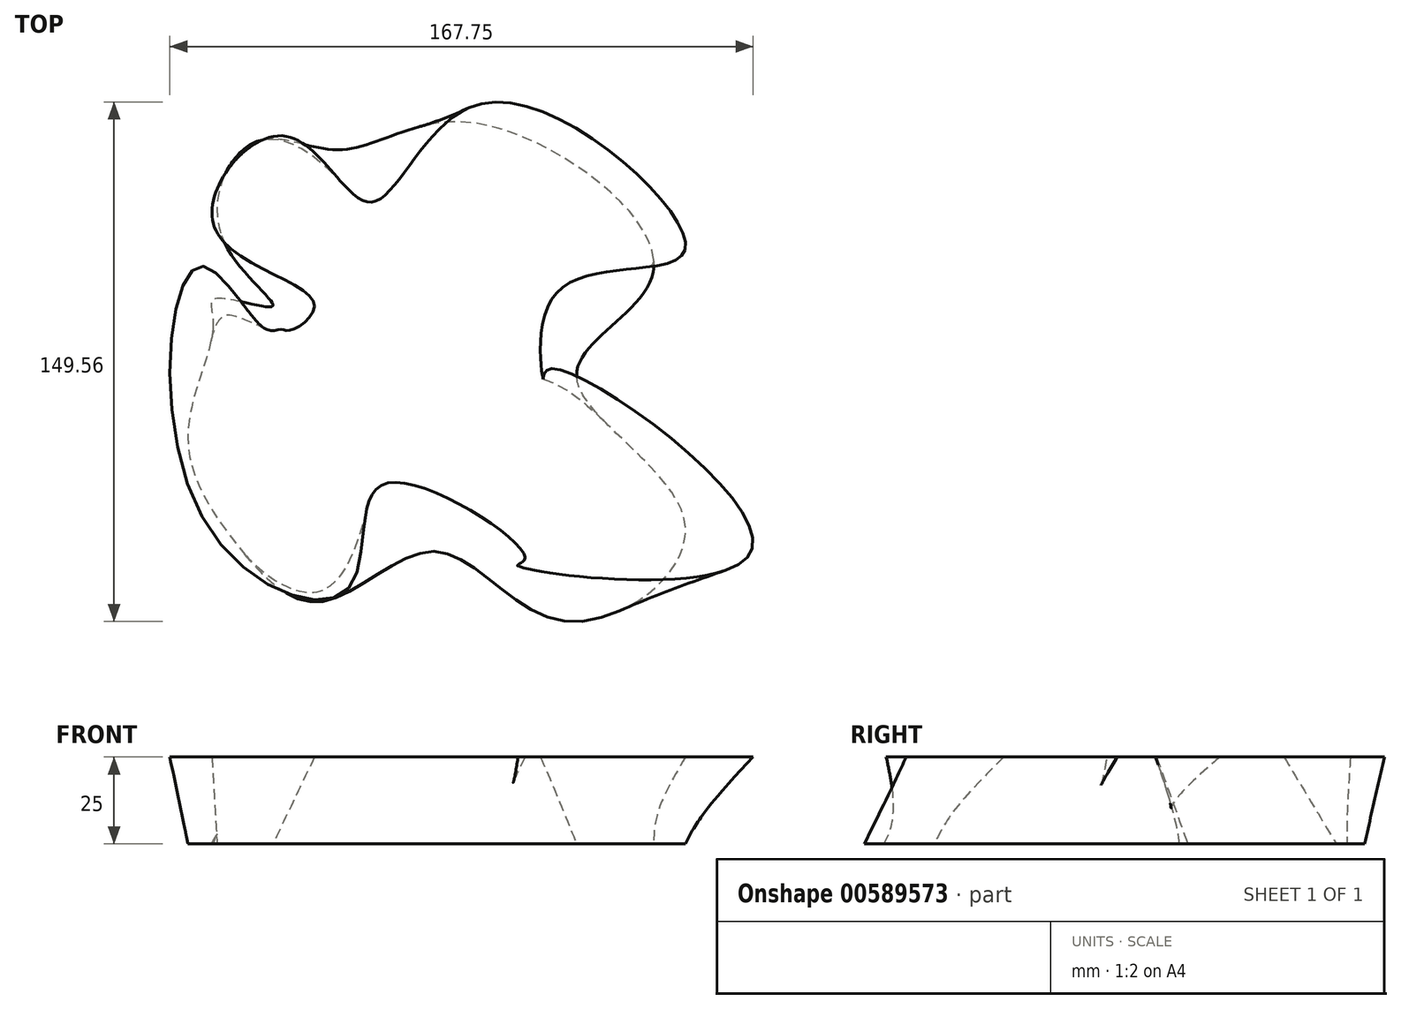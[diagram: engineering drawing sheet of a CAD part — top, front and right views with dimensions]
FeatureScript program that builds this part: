
annotation { "Feature Type Name" : "Feature", "Feature Type Description" : "" }
export const myFeature = defineFeature(function(context is Context, id is Id, definition is map)
    precondition{}
    {
        {
            var Q0;
            Q0=qCreatedBy(makeId("Top.planeOp"),FACE);
            var sketch = newSketch(context, id + "F0", { "sketchPlane" : qUnion([Q0])});
            skFitSpline(sketch, "E0", {"points": [v(-64.21, 14.7) * mm, v(-71.49, -17.14) * mm, v(-56.75, -49.56) * mm, v(-32.77, -65.19) * mm, v(0, -50.8) * mm, v(37.21, -70.84) * mm, v(71.54, -42.87) * mm, v(40.32, 0) * mm, v(62.5, 30.5) * mm, v(10.55, 72.58) * mm, v(-27.5, 64.81) * mm, v(-51.9, 67.12) * mm, v(-61.75, 39.97) * mm, v(-47.24, 19.73) * mm, v(-63.7, 21.93) * mm, v(-64.21, 14.7) * mm]});
            skSolve(sketch);
        }
        {
            var Q0;
            Q0=qCreatedBy(makeId("Top.planeOp"),FACE);
            var sketch = newSketch(context, id + "F1", { "sketchPlane" : qUnion([Q0])});
            skFitSpline(sketch, "E1", {"points": [v(-44.88, 13.13) * mm, v(-60.17, 17.93) * mm, v(-58.25, -33.6) * mm, v(-27.73, -52.66) * mm, v(-9.93, -41.15) * mm, v(24.33, -53.4) * mm, v(24.81, -53.92) * mm, v(60.55, -41.01) * mm, v(31.76, 0) * mm, v(31.29, 0) * mm, v(38.41, 18.86) * mm, v(55.85, 38.02) * mm, v(16.95, 65.75) * mm, v(-20.48, 57.4) * mm, v(-43.67, 61.7) * mm, v(-55.19, 44.27) * mm, v(-40.17, 18.9) * mm, v(-44.88, 13.13) * mm]});
            skSolve(sketch);
        }
        {
            var Q0;
            Q0=makeQuery(id+"F1.imprint","IMPRINT",FACE,{"disambiguationData":[TD([[makeQuery(id+"F1.imprint","IMPRINT",EDGE,{"derivedFrom":sQuery(id+"F1.wireOp",EDGE,"E1")}),1.0]])]});
            var sketch = newSketch(context, id + "F2", { "sketchPlane" : qUnion([Q0])});
            skFitSpline(sketch, "E2", {"points": [v(-55.12, -27.92) * mm, v(-36.05, -43.18) * mm, v(-20.66, -32.22) * mm, v(3.78, -34.26) * mm, v(21.3, -43.31) * mm, v(44.5, -27.21) * mm, v(22.15, 0) * mm, v(21.68, 0) * mm, v(25.22, 17.76) * mm, v(47.2, 37.9) * mm, v(18.96, 59.02) * mm, v(-7, 50.01) * mm, v(-35.2, 53.87) * mm, v(-35.68, 54.4) * mm, v(-48.96, 40.69) * mm, v(-30.49, 18.82) * mm, v(-38.83, 4.74) * mm, v(-55.57, 7.94) * mm, v(-57.66, -18.36) * mm, v(-55.12, -27.92) * mm]});
            skSolve(sketch);
        }
        {
            var Q0;
            Q0=makeQuery(id+"F2.imprint","IMPRINT",FACE,{"disambiguationData":[TD([[makeQuery(id+"F2.imprint","IMPRINT",EDGE,{"derivedFrom":sQuery(id+"F2.wireOp",EDGE,"E2")}),1.0]])]});
            var sketch = newSketch(context, id + "F3", { "sketchPlane" : qUnion([Q0])});
            skFitSpline(sketch, "E3", {"points": [v(-30.02, 26.93) * mm, v(-13.47, 36.18) * mm, v(14.32, 21.88) * mm, v(12.16, 6.54) * mm, v(23.9, -14.38) * mm, v(0, -23.71) * mm, v(-14.9, -11.72) * mm, v(-28.48, 0) * mm, v(-19.29, 9.38) * mm, v(-28.89, 22.07) * mm, v(-30.02, 26.93) * mm]});
            skSolve(sketch);
        }
        {
            var Q0;
            Q0=qCreatedBy(makeId("Top.planeOp"),FACE);
            cPlane(context, id + "F4", {"entities" : qUnion([Q0]), "cplaneType" : CPlaneType.OFFSET, "offset" : 25 * mm, "width" : 150 * mm, "height" : 150 * mm});
        }
        {
            var Q0;
            Q0=qCreatedBy(id+"F4.planeOp",FACE);
            var sketch = newSketch(context, id + "F5", { "sketchPlane" : qUnion([Q0])});
            skFitSpline(sketch, "E4.0", {"points": [v(-44.88, 13.13) * mm, v(-49.45, 13.42) * mm, v(-67.71, 31.28) * mm, v(-67.6, -40.47) * mm, v(-25.02, -61.05) * mm, v(-14.86, -31.3) * mm, v(25.52, -52.78) * mm, v(23.48, -54.78) * mm, v(90.55, -50.74) * mm, v(32.37, 1.77) * mm, v(30.73, -1.15) * mm, v(34.82, 23.95) * mm, v(71.43, 35.84) * mm, v(14.62, 78.41) * mm, v(-18.94, 49.75) * mm, v(-43.82, 68.81) * mm, v(-63.87, 42.67) * mm, v(-35.22, 20.83) * mm, v(-41.77, 12.93) * mm, v(-44.88, 13.13) * mm]});
            skSolve(sketch);
        }
        {
            var Q0;
            Q0=qCreatedBy(id+"F4.planeOp",FACE);
            cPlane(context, id + "F6", {"entities" : qUnion([Q0]), "cplaneType" : CPlaneType.OFFSET, "offset" : 25 * mm, "width" : 150 * mm, "height" : 150 * mm});
        }
        {
            var Q0;
            Q0=qCreatedBy(id+"F6.planeOp",FACE);
            cPlane(context, id + "F7", {"entities" : qUnion([Q0]), "cplaneType" : CPlaneType.OFFSET, "offset" : 25 * mm, "width" : 150 * mm, "height" : 150 * mm});
        }
        {
            var Q0;
            Q0=makeQuery(id+"F0.imprint","IMPRINT",FACE,{"disambiguationData":[TD([[makeQuery(id+"F0.imprint","IMPRINT",EDGE,{"derivedFrom":sQuery(id+"F0.wireOp",EDGE,"E0")}),1.0]])]});
            var Q1;
            Q1=makeQuery(id+"F5.imprint","IMPRINT",FACE,{"disambiguationData":[TD([[makeQuery(id+"F5.imprint","IMPRINT",EDGE,{"derivedFrom":sQuery(id+"F5.wireOp",EDGE,"E4.0")}),1.0]])]});
            loft(context, id + "F8", {"sheetProfilesArray" : [{ "sheetProfileEntities" : qUnion([Q0]) }, { "sheetProfileEntities" : qUnion([Q1]) }]});
        }
    });
